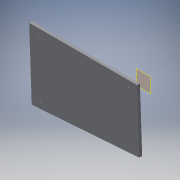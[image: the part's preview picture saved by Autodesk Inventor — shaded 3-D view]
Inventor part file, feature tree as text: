
AUTODESK INVENTOR PART (.ipt)
format: ipt  version: 2019.2 (Build 232265000, 265)  size: 104,960 bytes
history: native  units: in
note: dims shown in document units (in); Inventor stores cm internally (conversion verified against a paired STEP export)
features: sketch x2, plane x1, extrude x1, hole x1
ambient origin geometry x8: Origin, YZ Plane, XZ Plane, XY Plane, X Axis, Y Axis, Z Axis, Center Point
bodies: Solid1 (feature_tree)
feature tree (5):
  plane  "Work Plane1"
  extrude  "Extrusion1"  Depth=0.1575in TaperAngle=0.0deg
  hole  "Hole1"  [1 undecoded]
  sketch  "Sketch2"  dims[d0=0.8125in d1=0.1575in d2=0.0in]
  sketch  "Sketch3"  dims[d3=0.0787in d4=0.75in d5=0.375in d6=0.25in d7=0.5635in d8=1.0in d9=0.8108in]
note: 1 required parameter value undecoded (feature->parameter linkage not recoverable at this tier; creation-order binding heuristic only, values carry confidence <= 0.55)
